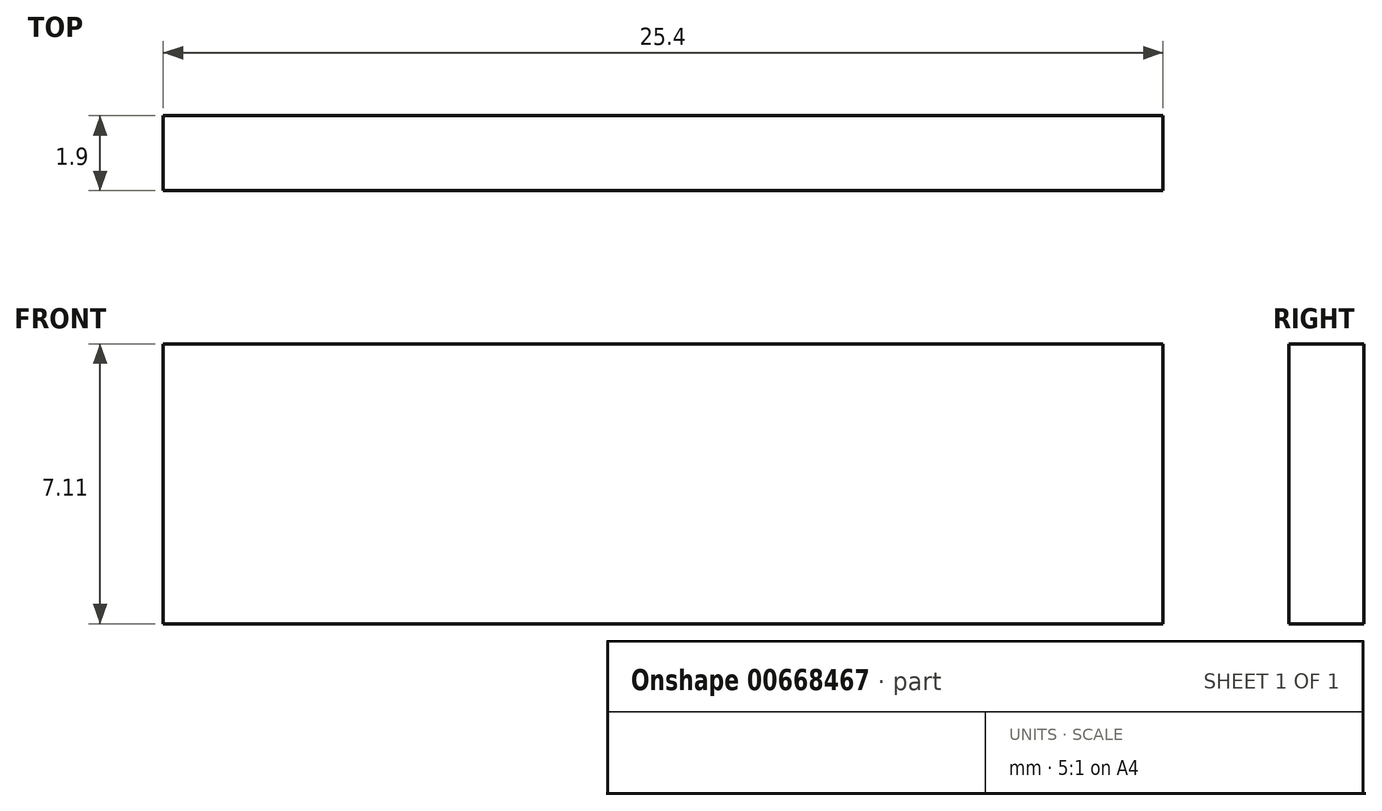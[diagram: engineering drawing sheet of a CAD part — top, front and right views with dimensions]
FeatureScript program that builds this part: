
annotation { "Feature Type Name" : "Feature", "Feature Type Description" : "" }
export const myFeature = defineFeature(function(context is Context, id is Id, definition is map)
    precondition{}
    {
        {
            var Q0;
            Q0=qCreatedBy(makeId("Front.planeOp"),FACE);
            var sketch = newSketch(context, id + "F0", { "sketchPlane" : qUnion([Q0])});
            skLineSegment(sketch, "E0.bottom", {"start": v(-25.4, 21.06) * mm, "end": v(0, 21.06) * mm});
            skLineSegment(sketch, "E0.top", {"start": v(-25.4, 13.95) * mm, "end": v(0, 13.95) * mm});
            skLineSegment(sketch, "E0.left", {"start": v(-25.4, 21.06) * mm, "end": v(-25.4, 13.95) * mm});
            skLineSegment(sketch, "E0.right", {"start": v(0, 21.06) * mm, "end": v(0, 13.95) * mm});
            skSolve(sketch);
        }
        {
            var Q0;
            Q0=makeQuery(id+"F0.imprint","IMPRINT",FACE,{"disambiguationData":[TD([[makeQuery(id+"F0.imprint","IMPRINT",EDGE,{"derivedFrom":sQuery(id+"F0.wireOp",EDGE,"E0.bottom")}),-1.0]])]});
            extrude(context, id + "F1", {"entities" : qUnion([Q0]), "depth" : 1.9 * mm});
        }
    });
